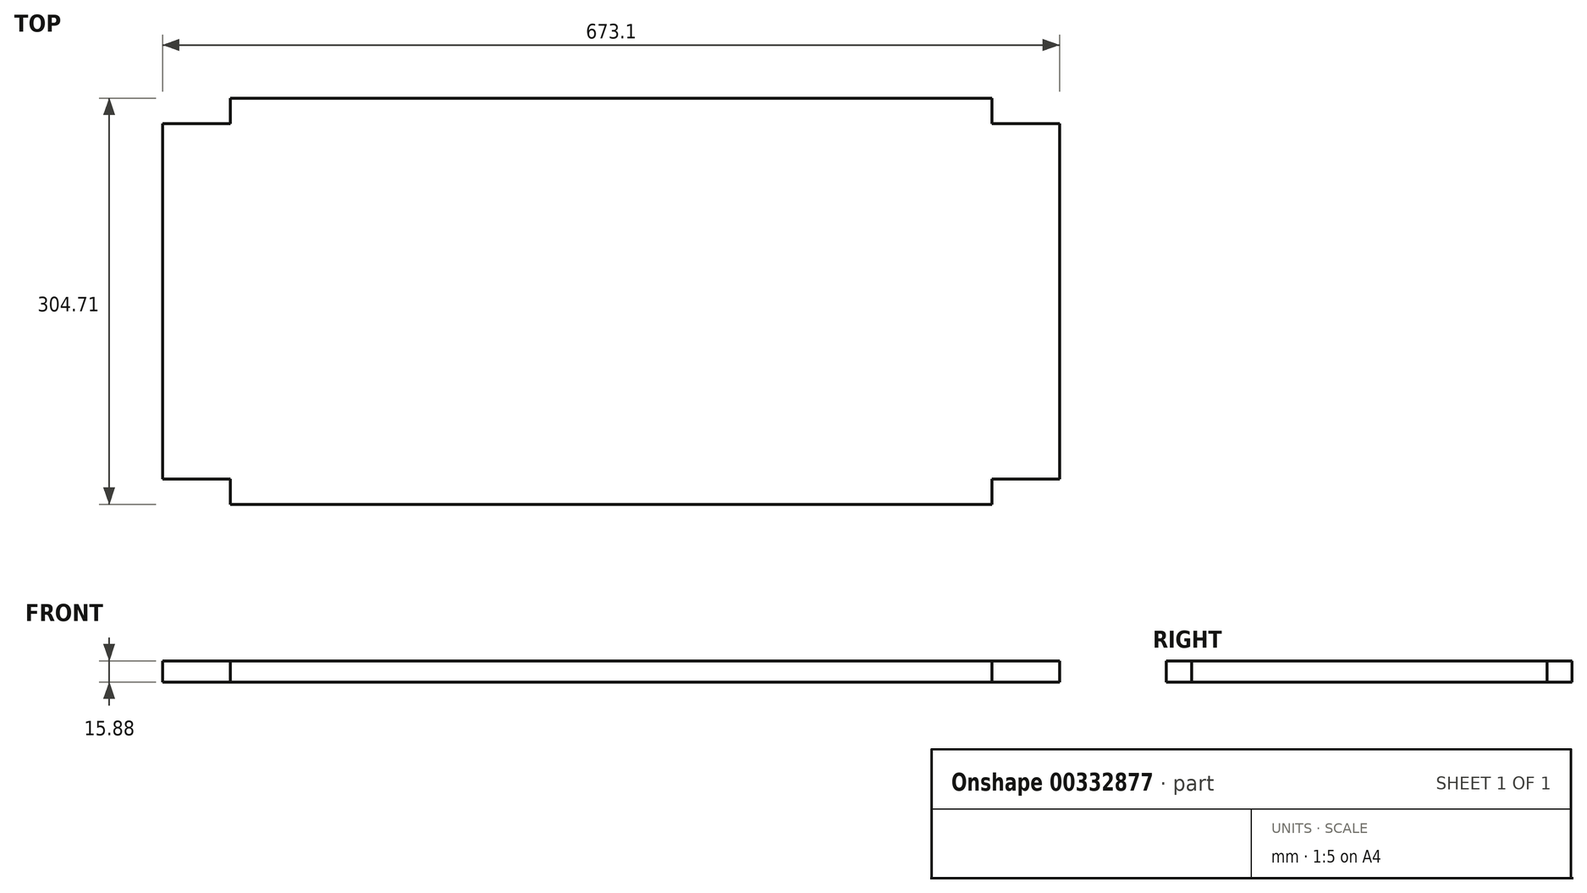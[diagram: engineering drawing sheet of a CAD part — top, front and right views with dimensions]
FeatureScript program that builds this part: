
annotation { "Feature Type Name" : "Feature", "Feature Type Description" : "" }
export const myFeature = defineFeature(function(context is Context, id is Id, definition is map)
    precondition{}
    {
        {
            var Q0;
            Q0=qCreatedBy(makeId("Top.planeOp"),FACE);
            var sketch = newSketch(context, id + "F0", { "sketchPlane" : qUnion([Q0])});
            skPoint(sketch, "E0.middle", {"position": v(0, 0) * mm});
            skLineSegment(sketch, "E1.top", {"start": v(736.6, 31.38) * mm, "end": v(685.8, 31.38) * mm});
            skLineSegment(sketch, "E1.right", {"start": v(685.8, 50.28) * mm, "end": v(685.8, 31.38) * mm});
            skLineSegment(sketch, "E2.bottom", {"start": v(685.8, -235.32) * mm, "end": v(736.6, -235.32) * mm});
            skLineSegment(sketch, "E2.left", {"start": v(685.8, -235.32) * mm, "end": v(685.8, -254.37) * mm});
            skPoint(sketch, "E3.trimOffspring.end.orphan", {"position": v(736.6, 254.37) * mm});
            skPoint(sketch, "E4.orphan", {"position": v(736.6, -254.37) * mm});
            skPoint(sketch, "E5.orphan", {"position": v(-736.6, -254.37) * mm});
            skPoint(sketch, "E6.orphan", {"position": v(-736.6, 254.37) * mm});
            skLineSegment(sketch, "E7", {"start": v(685.8, 50.28) * mm, "end": v(114.3, 50.34) * mm});
            skLineSegment(sketch, "E8.bottom", {"start": v(63.5, 31.38) * mm, "end": v(114.3, 31.38) * mm});
            skLineSegment(sketch, "E8.right", {"start": v(114.3, 31.38) * mm, "end": v(114.3, 50.34) * mm});
            skLineSegment(sketch, "E9.bottom", {"start": v(63.5, -235.32) * mm, "end": v(114.3, -235.32) * mm});
            skLineSegment(sketch, "E9.right", {"start": v(114.3, -235.32) * mm, "end": v(114.3, -254.37) * mm});
            skLineSegment(sketch, "E10.trimOffspring", {"start": v(114.3, -254.37) * mm, "end": v(685.8, -254.37) * mm});
            skLineSegment(sketch, "E11", {"start": v(736.6, 31.38) * mm, "end": v(736.6, -235.32) * mm});
            skPoint(sketch, "E12.orphan", {"position": v(-936.62, -254.37) * mm});
            skLineSegment(sketch, "E13", {"start": v(63.5, 31.38) * mm, "end": v(63.5, -235.32) * mm});
            skPoint(sketch, "E14.right.start.orphan", {"position": v(-685.8, 50.43) * mm});
            skPoint(sketch, "E14.top.end.orphan", {"position": v(-685.8, 31.38) * mm});
            skPoint(sketch, "E15.end.orphan", {"position": v(-736.6, 31.38) * mm});
            skPoint(sketch, "E16.bottom.start.orphan", {"position": v(-736.6, 50.43) * mm});
            skPoint(sketch, "E17.bottom.start.orphan", {"position": v(-927.1, 31.38) * mm});
            skPoint(sketch, "E18.right.end.orphan", {"position": v(-927.1, -235.32) * mm});
            skPoint(sketch, "E19.bottom.end.orphan", {"position": v(-736.6, -235.32) * mm});
            skPoint(sketch, "E19.left.start.orphan", {"position": v(-685.8, -235.32) * mm});
            skSolve(sketch);
        }
        {
            var Q0;
            Q0=qSketchRegion(id+"F0",true);
            extrude(context, id + "F1", {"entities" : qUnion([Q0]), "depth" : 15.88 * mm});
        }
    });
